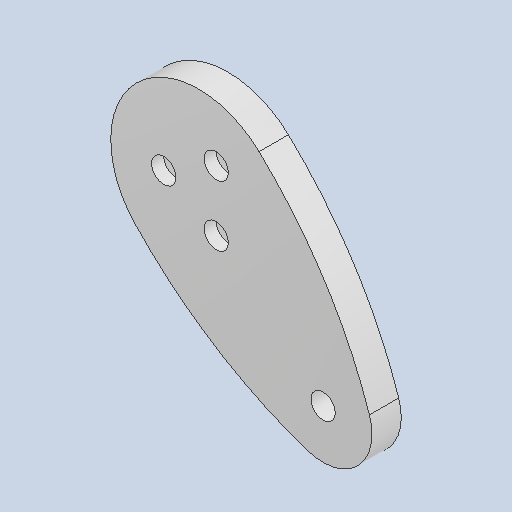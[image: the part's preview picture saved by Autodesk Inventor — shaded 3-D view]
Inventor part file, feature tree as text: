
AUTODESK INVENTOR PART (.ipt)
format: ipt  version: 2023 (Build 270158030, 158C)  size: 147,968 bytes
history: native  units: mm
features: other x3, sketch x2
ambient origin geometry x8: Origin, YZ Plane, XZ Plane, XY Plane, X Axis, Y Axis, Z Axis, Center Point
bodies: Solid2 (feature_tree)
feature tree (5):
  other  "クランク_前.ipt"
  other  "Solid2::クランク_前.ipt"
  other  "TaggingFeature1"
  sketch  "Sketch2"  dims[d0=10.0mm]
  sketch  "Sketch3"
